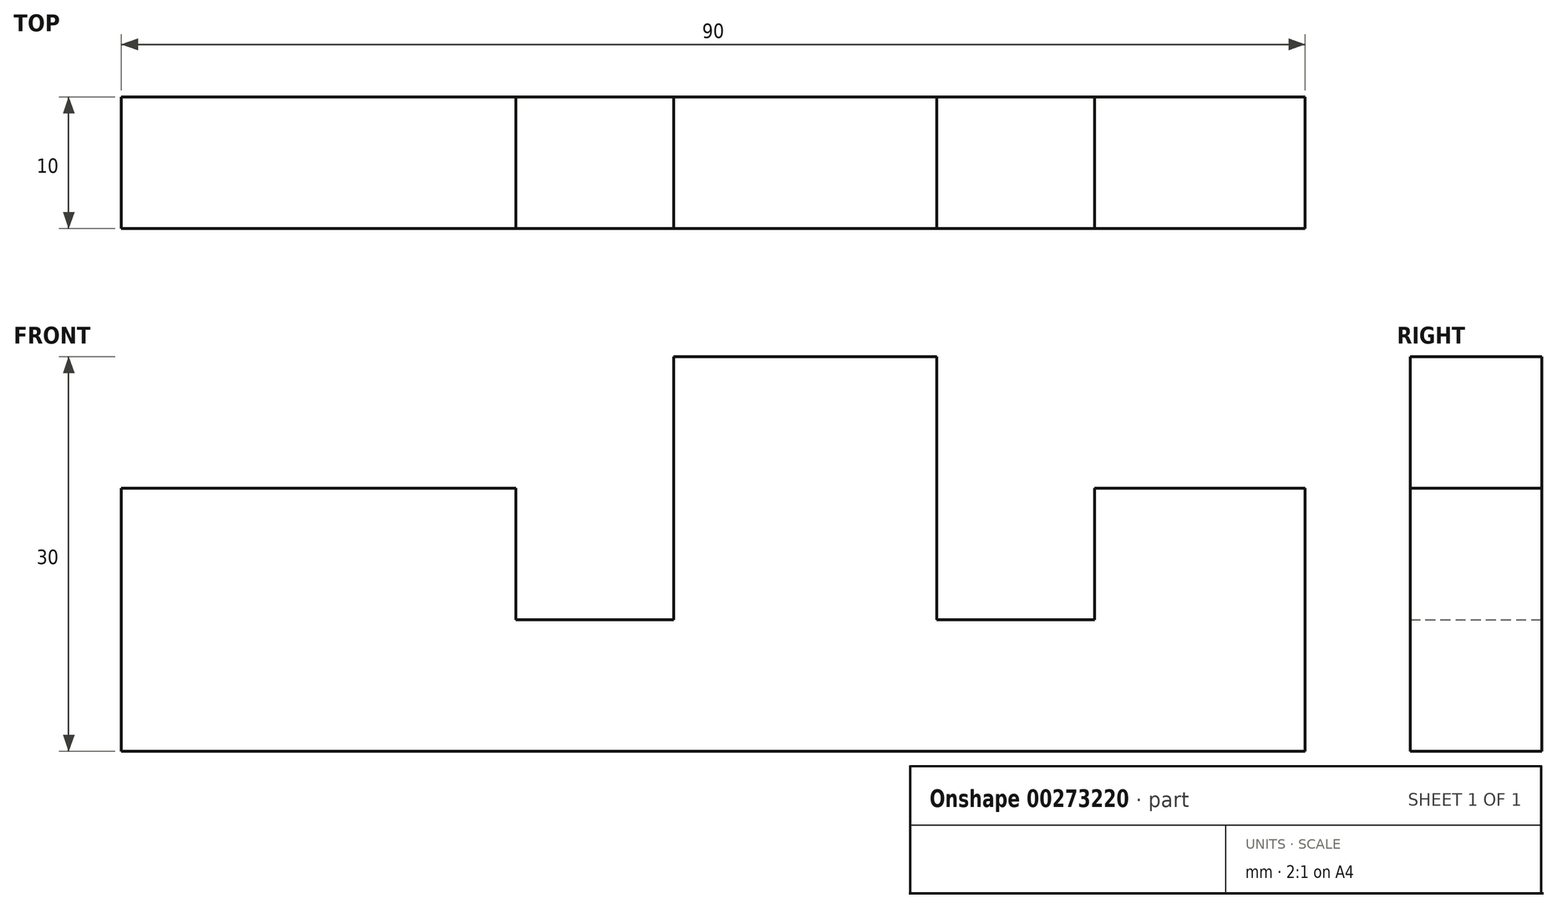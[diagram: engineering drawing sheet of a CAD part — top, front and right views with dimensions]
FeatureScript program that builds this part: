
annotation { "Feature Type Name" : "Feature", "Feature Type Description" : "" }
export const myFeature = defineFeature(function(context is Context, id is Id, definition is map)
    precondition{}
    {
        {
            var Q0;
            Q0=qCreatedBy(makeId("Front.planeOp"),FACE);
            var sketch = newSketch(context, id + "F0", { "sketchPlane" : qUnion([Q0])});
            skLineSegment(sketch, "E0", {"start": v(0, 0) * mm, "end": v(90, 0) * mm});
            skLineSegment(sketch, "E1", {"start": v(0, 0) * mm, "end": v(0, 20) * mm});
            skLineSegment(sketch, "E2", {"start": v(0, 20) * mm, "end": v(30, 20) * mm});
            skLineSegment(sketch, "E3", {"start": v(42, 30) * mm, "end": v(42, 10) * mm});
            skLineSegment(sketch, "E4", {"start": v(42, 10) * mm, "end": v(30, 10) * mm});
            skLineSegment(sketch, "E5", {"start": v(30, 10) * mm, "end": v(30, 20) * mm});
            skLineSegment(sketch, "E6", {"start": v(42, 30) * mm, "end": v(62, 30) * mm});
            skLineSegment(sketch, "E7", {"start": v(62, 30) * mm, "end": v(62, 10) * mm});
            skLineSegment(sketch, "E8", {"start": v(62, 10) * mm, "end": v(74, 10) * mm});
            skLineSegment(sketch, "E9", {"start": v(74, 10) * mm, "end": v(74, 20) * mm});
            skLineSegment(sketch, "E10", {"start": v(74, 20) * mm, "end": v(90, 20) * mm});
            skLineSegment(sketch, "E11", {"start": v(90, 20) * mm, "end": v(90, 0) * mm});
            skLineSegment(sketch, "E12", {"start": v(30, 20) * mm, "end": v(74, 20) * mm, "construction": true});
            skSolve(sketch);
        }
        {
            var Q0;
            Q0 = qSketchRegion(id + "F0", true);
            extrude(context, id + "F1", {"entities" : qUnion([Q0]), "depth" : 10 * mm});
        }
    });
